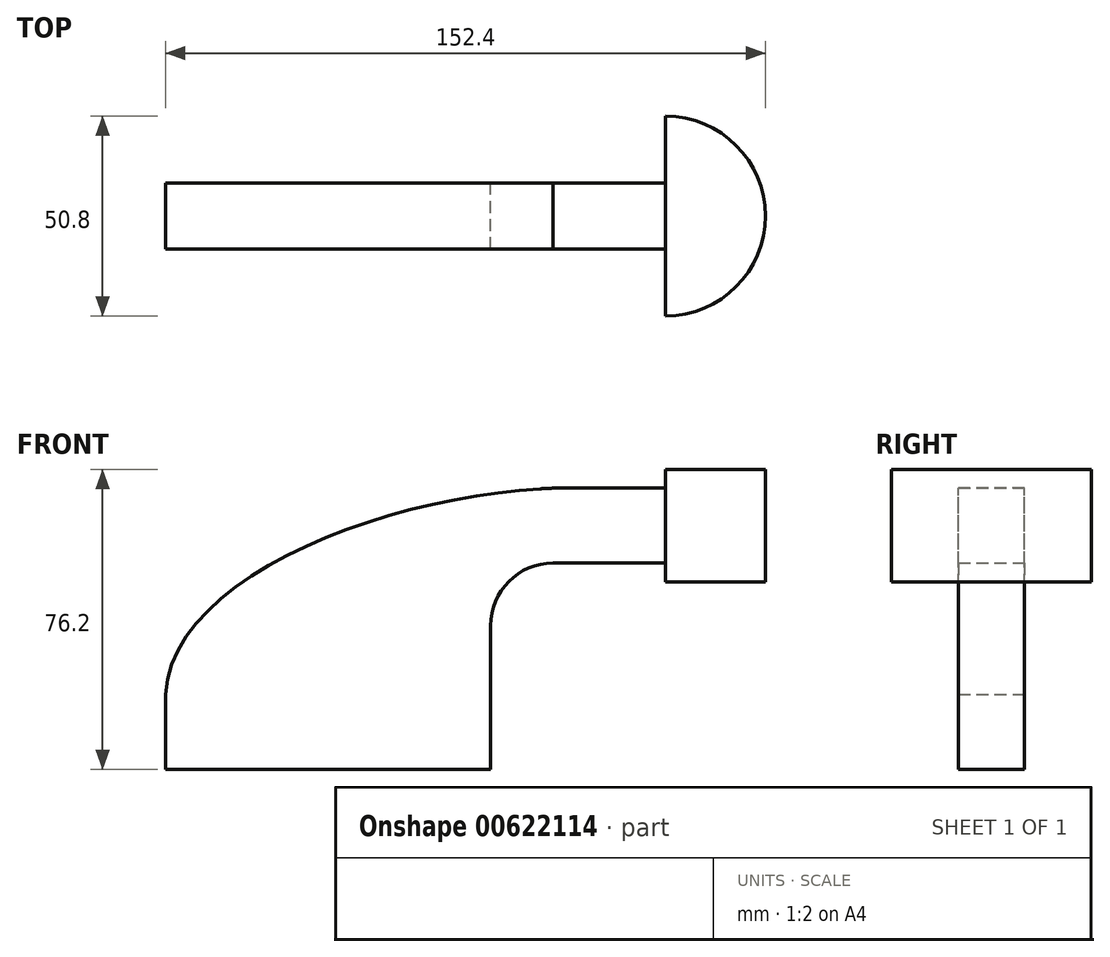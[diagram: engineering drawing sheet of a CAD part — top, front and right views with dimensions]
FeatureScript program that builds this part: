
annotation { "Feature Type Name" : "Feature", "Feature Type Description" : "" }
export const myFeature = defineFeature(function(context is Context, id is Id, definition is map)
    precondition{}
    {
        {
            var Q0;
            Q0=qCreatedBy(makeId("Front.planeOp"),FACE);
            var sketch = newSketch(context, id + "F0", { "sketchPlane" : qUnion([Q0])});
            skLineSegment(sketch, "E0.rect.bottom", {"start": v(-41.28, 9.52) * mm, "end": v(41.28, 9.52) * mm});
            skLineSegment(sketch, "E0.rect.top", {"start": v(-41.28, -9.52) * mm, "end": v(41.28, -9.52) * mm});
            skLineSegment(sketch, "E0.rect.left", {"start": v(-41.28, 9.52) * mm, "end": v(-41.28, -9.52) * mm});
            skLineSegment(sketch, "E0.rect.right", {"start": v(41.28, 9.52) * mm, "end": v(41.28, -9.52) * mm});
            skPoint(sketch, "E0.rect.middle", {"position": v(0, 0) * mm});
            skLineSegment(sketch, "E1", {"start": v(41.28, 9.52) * mm, "end": v(41.28, 27) * mm});
            skArc(sketch, "E2", {"start": v(41.28, 27) * mm, "mid": v(45.92, 38.23) * mm, "end": v(57.15, 42.88) * mm});
            skLineSegment(sketch, "E3", {"start": v(57.15, 42.88) * mm, "end": v(85.72, 42.88) * mm});
            skLineSegment(sketch, "E4.rect.bottom", {"start": v(60.32, 38.1) * mm, "end": v(111.12, 38.1) * mm});
            skLineSegment(sketch, "E4.rect.top", {"start": v(60.32, 66.68) * mm, "end": v(111.12, 66.68) * mm});
            skLineSegment(sketch, "E4.rect.left", {"start": v(60.32, 38.1) * mm, "end": v(60.32, 66.68) * mm});
            skLineSegment(sketch, "E4.rect.right", {"start": v(111.13, 38.1) * mm, "end": v(111.12, 66.68) * mm});
            skPoint(sketch, "E4.rect.middle", {"position": v(85.72, 52.39) * mm});
            skLineSegment(sketch, "E5.0", {"start": v(57.15, 61.93) * mm, "end": v(85.72, 61.93) * mm});
            skArc(sketch, "E5.1", {"start": v(22.23, 27) * mm, "mid": v(32.45, 51.7) * mm, "end": v(57.15, 61.93) * mm});
            skLineSegment(sketch, "E5.2", {"start": v(22.23, 9.52) * mm, "end": v(22.23, 27) * mm});
            skLineSegment(sketch, "E6", {"start": v(85.72, 38.1) * mm, "end": v(85.72, 66.68) * mm});
            skFitSpline(sketch, "E7", {"points": [v(-41.28, 9.53) * mm, v(57.15, 61.93) * mm], "startDerivative": vector(5.2, 92.34) * mm, "endDerivative": vector(120.92, 4.22) * mm});
            skSolve(sketch);
        }
        {
            var Q0;
            Q0=makeQuery(id+"F0.imprint","IMPRINT",FACE,{"disambiguationData":[TD([[makeQuery(id+"F0.imprint","IMPRINT",EDGE,{"derivedFrom":sQuery(id+"F0.wireOp",EDGE,"E0.rect.top")}),1.0]])]});
            var Q1;
            {var subQ3=sQuery(id+"F0.wireOp",EDGE,"E5.2");Q1=makeQuery(id+"F0.imprint","IMPRINT",FACE,{"disambiguationData":[TD([[makeQuery(id+"F0.imprint","IMPRINT",EDGE,{"derivedFrom":subQ3}),1.0]])]});}
            var Q2;
            {var subQ4=sQuery(id+"F0.wireOp",EDGE,"E1");Q2=makeQuery(id+"F0.imprint","IMPRINT",FACE,{"disambiguationData":[TD([[makeQuery(id+"F0.imprint","IMPRINT",EDGE,{"derivedFrom":subQ4}),1.0]])]});}
            var Q3;
            {var subQ0=sQuery(id+"F0.wireOp",EDGE,"E6");var subQ1=sQuery(id+"F0.wireOp",EDGE,"E3");var subQ2=makeQuery(id+"F0.imprint","INTERSECT",VERTEX,{"derivedFrom":[subQ1,subQ0]});Q3=makeQuery(id+"F0.imprint","IMPRINT",FACE,{"disambiguationData":[TD([[makeQuery(id+"F0.imprint","IMPRINT",EDGE,{"disambiguationData":[TD([[subQ2,1.0]])],"derivedFrom":subQ1}),1.0]])]});}
            extrude(context, id + "F1", {"entities" : qUnion([Q0, Q1, Q2, Q3]), "endBound" : BoundingType.SYMMETRIC, "depth" : 16.76 * mm, "offsetDistance" : 25.4 * mm});
        }
        {
            var Q0;
            {var subQ0=sQuery(id+"F0.wireOp",EDGE,"E4.rect.right");Q0=makeQuery(id+"F0.imprint","IMPRINT",FACE,{"disambiguationData":[TD([[makeQuery(id+"F0.imprint","IMPRINT",EDGE,{"derivedFrom":subQ0}),1.0]])]});}
            var Q1;
            Q1=sQuery(id+"F0.wireOp",EDGE,"E6");
            revolve(context, id + "F2", {"entities" : qUnion([Q0]), "axis" : qUnion([Q1]), "revolveType" : RevolveType.SYMMETRIC, "angle" : 180 * degree});
        }
    });
